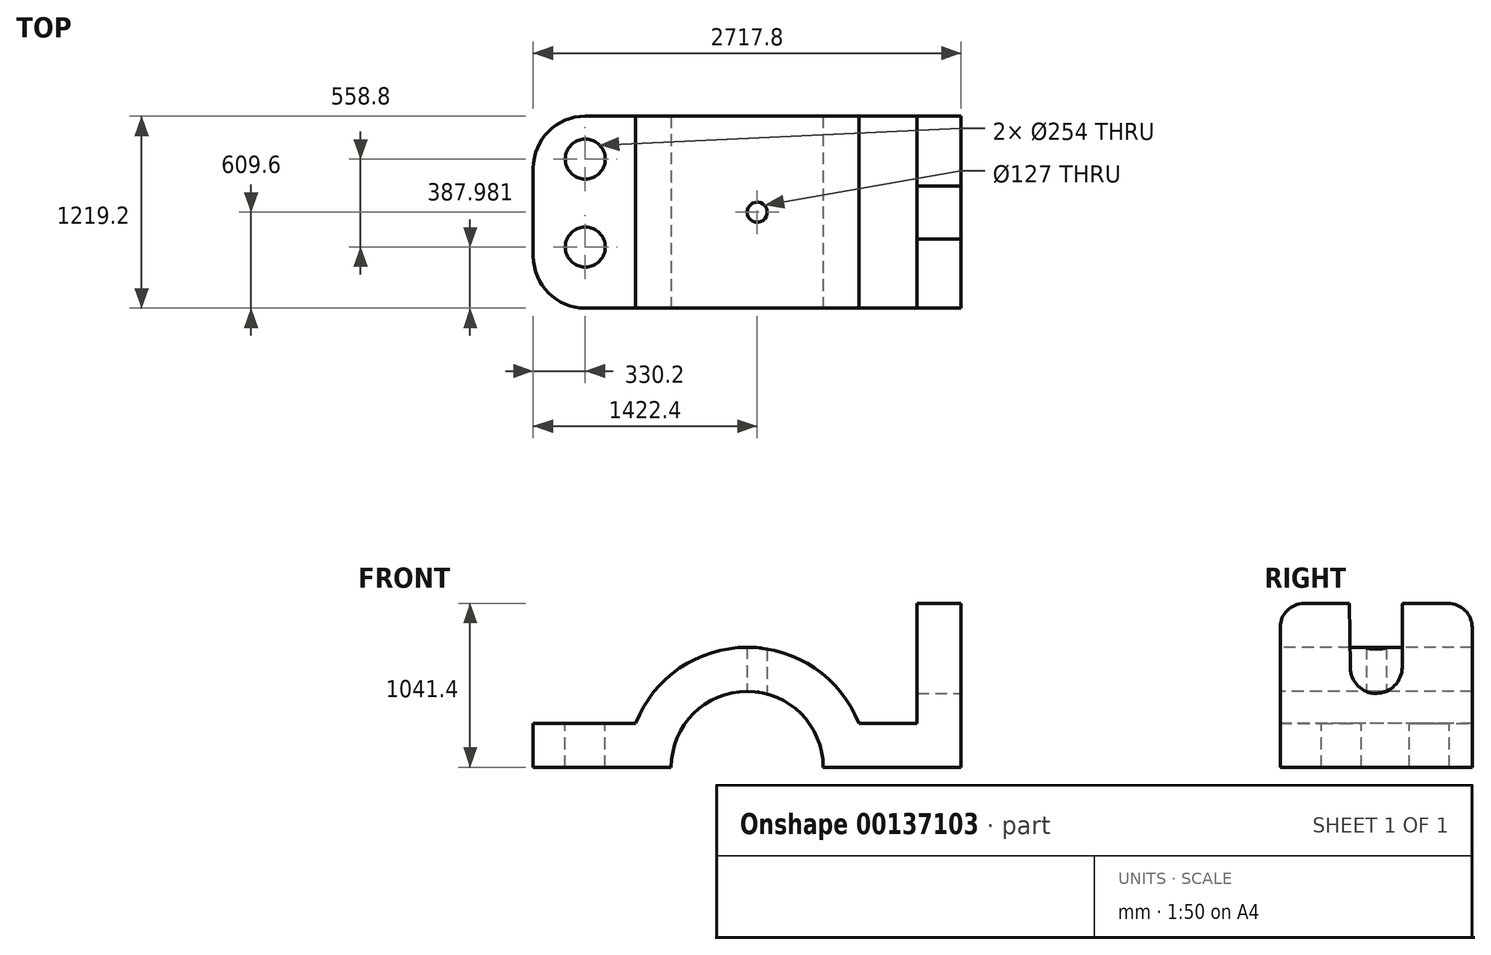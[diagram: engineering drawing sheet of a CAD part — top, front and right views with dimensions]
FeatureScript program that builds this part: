
annotation { "Feature Type Name" : "Feature", "Feature Type Description" : "" }
export const myFeature = defineFeature(function(context is Context, id is Id, definition is map)
    precondition{}
    {
        {
            var Q0;
            Q0=qCreatedBy(makeId("Front.planeOp"),FACE);
            var sketch = newSketch(context, id + "F0", { "sketchPlane" : qUnion([Q0])});
            skLineSegment(sketch, "E0", {"start": v(0, 0) * mm, "end": v(2717.8, 0) * mm});
            skLineSegment(sketch, "E1", {"start": v(2717.8, 0) * mm, "end": v(2717.8, 1041.4) * mm});
            skLineSegment(sketch, "E2", {"start": v(2717.8, 1041.4) * mm, "end": v(0, 1041.4) * mm});
            skLineSegment(sketch, "E3", {"start": v(0, 1041.4) * mm, "end": v(0, 0) * mm});
            skSolve(sketch);
        }
        {
            var Q0;
            Q0 = qSketchRegion(id + "F0", true);
            extrude(context, id + "F1", {"entities" : qUnion([Q0]), "depth" : 1219.2 * mm});
        }
        {
            var Q0;
            Q0=makeQuery(id+"F1.opExtrude","CAP_FACE",FACE,{"disambiguationData":[OSD([sQuery(id+"F0.wireOp",EDGE,"E0"),sQuery(id+"F0.wireOp",EDGE,"E1"),sQuery(id+"F0.wireOp",EDGE,"E2"),sQuery(id+"F0.wireOp",EDGE,"E3")])],"isStart":false});
            var sketch = newSketch(context, id + "F2", { "sketchPlane" : qUnion([Q0])});
            skArc(sketch, "E4", {"start": v(2067.83, 279.4) * mm, "mid": v(1358.9, 762) * mm, "end": v(649.97, 279.4) * mm});
            skArc(sketch, "E5", {"start": v(1841.5, 0) * mm, "mid": v(1358.9, 482.6) * mm, "end": v(876.3, 0) * mm});
            skLineSegment(sketch, "E6", {"start": v(0, 0) * mm, "end": v(0, 279.4) * mm});
            skLineSegment(sketch, "E7", {"start": v(0, 279.4) * mm, "end": v(649.97, 279.4) * mm});
            skLineSegment(sketch, "E8", {"start": v(2438.4, 279.4) * mm, "end": v(2067.83, 279.4) * mm});
            skPoint(sketch, "E8.startSnap0", {"position": v(324.99, 279.4) * mm});
            skLineSegment(sketch, "E9", {"start": v(2438.4, 279.4) * mm, "end": v(2438.4, 1041.4) * mm});
            skLineSegment(sketch, "E10", {"start": v(2438.4, 1041.4) * mm, "end": v(2717.8, 1041.4) * mm});
            skPoint(sketch, "E11.start.orphan", {"position": v(2717.8, 279.4) * mm});
            skPoint(sketch, "E12.start.orphan", {"position": v(2717.8, 0) * mm});
            skPoint(sketch, "E13.orphan", {"position": v(2438.4, 0) * mm});
            skLineSegment(sketch, "E14", {"start": v(0, 0) * mm, "end": v(876.3, 0) * mm});
            skLineSegment(sketch, "E15", {"start": v(1841.5, 0) * mm, "end": v(2717.8, 0) * mm});
            skLineSegment(sketch, "E16", {"start": v(2717.8, 1041.4) * mm, "end": v(2717.8, 0) * mm});
            skSolve(sketch);
        }
        {
            var Q0;
            Q0=makeQuery(id+"F2.imprint","IMPRINT",FACE,{"disambiguationData":[TD([[makeQuery(id+"F2.imprint","IMPRINT",EDGE,{"derivedFrom":sQuery(id+"F2.wireOp",EDGE,"E4")}),-1.0]])]});
            extrude(context, id + "F3", {"entities" : qUnion([Q0]), "operationType" : NewBodyOperationType.REMOVE, "oppositeDirection" : true, "depth" : 1541.08 * mm});
        }
        {
            var Q0;
            Q0=makeQuery(id+"F1.opExtrude","CAP_FACE",FACE,{"disambiguationData":[OSD([sQuery(id+"F0.wireOp",EDGE,"E0"),sQuery(id+"F0.wireOp",EDGE,"E1"),sQuery(id+"F0.wireOp",EDGE,"E2"),sQuery(id+"F0.wireOp",EDGE,"E3")])],"isStart":false});
            var sketch = newSketch(context, id + "F4", { "sketchPlane" : qUnion([Q0])});
            skCircle(sketch, "E17", {"center": v(1358.9, 0) * mm, "radius": 482.6 * mm});
            skSolve(sketch);
        }
        {
            var Q0;
            Q0 = qSketchRegion(id + "F4", true);
            extrude(context, id + "F5", {"entities" : qUnion([Q0]), "operationType" : NewBodyOperationType.REMOVE, "oppositeDirection" : true, "depth" : 1219.2 * mm});
        }
        {
            var Q0;
            Q0=makeQuery(id+"F3.boolean.opBoolean","COPY",FACE,{"derivedFrom":makeQuery(id+"F3.opExtrude","SWEPT_FACE",FACE,{"disambiguationData":[OSD([sQuery(id+"F2.wireOp",EDGE,"E7")])]})});
            var sketch = newSketch(context, id + "F6", { "sketchPlane" : qUnion([Q0])});
            skCircle(sketch, "E18", {"center": v(330.2, -272.42) * mm, "radius": 127 * mm});
            skCircle(sketch, "E19", {"center": v(330.2, -831.22) * mm, "radius": 127 * mm});
            skSolve(sketch);
        }
        {
            var Q0;
            Q0 = qSketchRegion(id + "F6", true);
            extrude(context, id + "F7", {"entities" : qUnion([Q0]), "operationType" : NewBodyOperationType.REMOVE, "oppositeDirection" : true, "depth" : 279.4 * mm});
        }
        {
            var Q0;
            {var subQ2=sQuery(id+"F0.wireOp",EDGE,"E1");var subQ3=sQuery(id+"F0.wireOp",EDGE,"E0");Q0=makeQuery(id+"F5.boolean.opBoolean","SPLIT",FACE,{"disambiguationData":[TD([makeQuery(id+"F1.opExtrude","SWEPT_FACE",FACE,{"disambiguationData":[OSD([subQ2])]})])],"derivedFrom":makeQuery(id+"F1.opExtrude","SWEPT_FACE",FACE,{"disambiguationData":[OSD([subQ3])]})});}
            var sketch = newSketch(context, id + "F8", { "sketchPlane" : qUnion([Q0])});
            skCircle(sketch, "E20", {"center": v(1422.4, 609.6) * mm, "radius": 63.5 * mm});
            skSolve(sketch);
        }
        {
            var Q0;
            Q0 = qSketchRegion(id + "F8", true);
            extrude(context, id + "F9", {"entities" : qUnion([Q0]), "operationType" : NewBodyOperationType.REMOVE, "oppositeDirection" : true, "depth" : 1270 * mm});
        }
        {
            var Q0;
            Q0=makeQuery(id+"F1.opExtrude","SWEPT_FACE",FACE,{"disambiguationData":[OSD([sQuery(id+"F0.wireOp",EDGE,"E1")])]});
            var sketch = newSketch(context, id + "F10", { "sketchPlane" : qUnion([Q0])});
            skArc(sketch, "E21", {"start": v(-774.7, 633.18) * mm, "mid": v(-608.7, 469.9) * mm, "end": v(-444.5, 635) * mm});
            skLineSegment(sketch, "E22", {"start": v(-779.18, 1041.4) * mm, "end": v(-774.7, 633.18) * mm});
            skLineSegment(sketch, "E23", {"start": v(-444.5, 1041.4) * mm, "end": v(-444.5, 635) * mm});
            skLineSegment(sketch, "E24", {"start": v(-779.18, 1041.4) * mm, "end": v(-444.5, 1041.4) * mm});
            skSolve(sketch);
        }
        {
            var Q0;
            Q0 = qSketchRegion(id + "F10", true);
            extrude(context, id + "F11", {"entities" : qUnion([Q0]), "operationType" : NewBodyOperationType.REMOVE, "oppositeDirection" : true, "depth" : 279.4 * mm});
        }
        {
            var Q0;
            Q0=makeQuery(id+"F1.opExtrude","CAP_EDGE",EDGE,{"disambiguationData":[OSD([sQuery(id+"F0.wireOp",EDGE,"E3")])],"isStart":true});
            var Q1;
            Q1=makeQuery(id+"F1.opExtrude","CAP_EDGE",EDGE,{"disambiguationData":[OSD([sQuery(id+"F0.wireOp",EDGE,"E3")])],"isStart":false});
            fillet(context, id + "F12", {"entities" : qUnion([Q0, Q1]), "radius" : 330.2 * mm, "tangentPropagation" : true, "allowEdgeOverflow" : false});
        }
        {
            var Q0;
            Q0=makeQuery(id+"F1.opExtrude","CAP_EDGE",EDGE,{"disambiguationData":[OSD([sQuery(id+"F0.wireOp",EDGE,"E2")])],"isStart":false});
            var Q1;
            Q1=makeQuery(id+"F1.opExtrude","CAP_EDGE",EDGE,{"disambiguationData":[OSD([sQuery(id+"F0.wireOp",EDGE,"E2")])],"isStart":true});
            fillet(context, id + "F13", {"entities" : qUnion([Q0, Q1]), "radius" : 152.4 * mm, "tangentPropagation" : true, "allowEdgeOverflow" : false});
        }
    });
